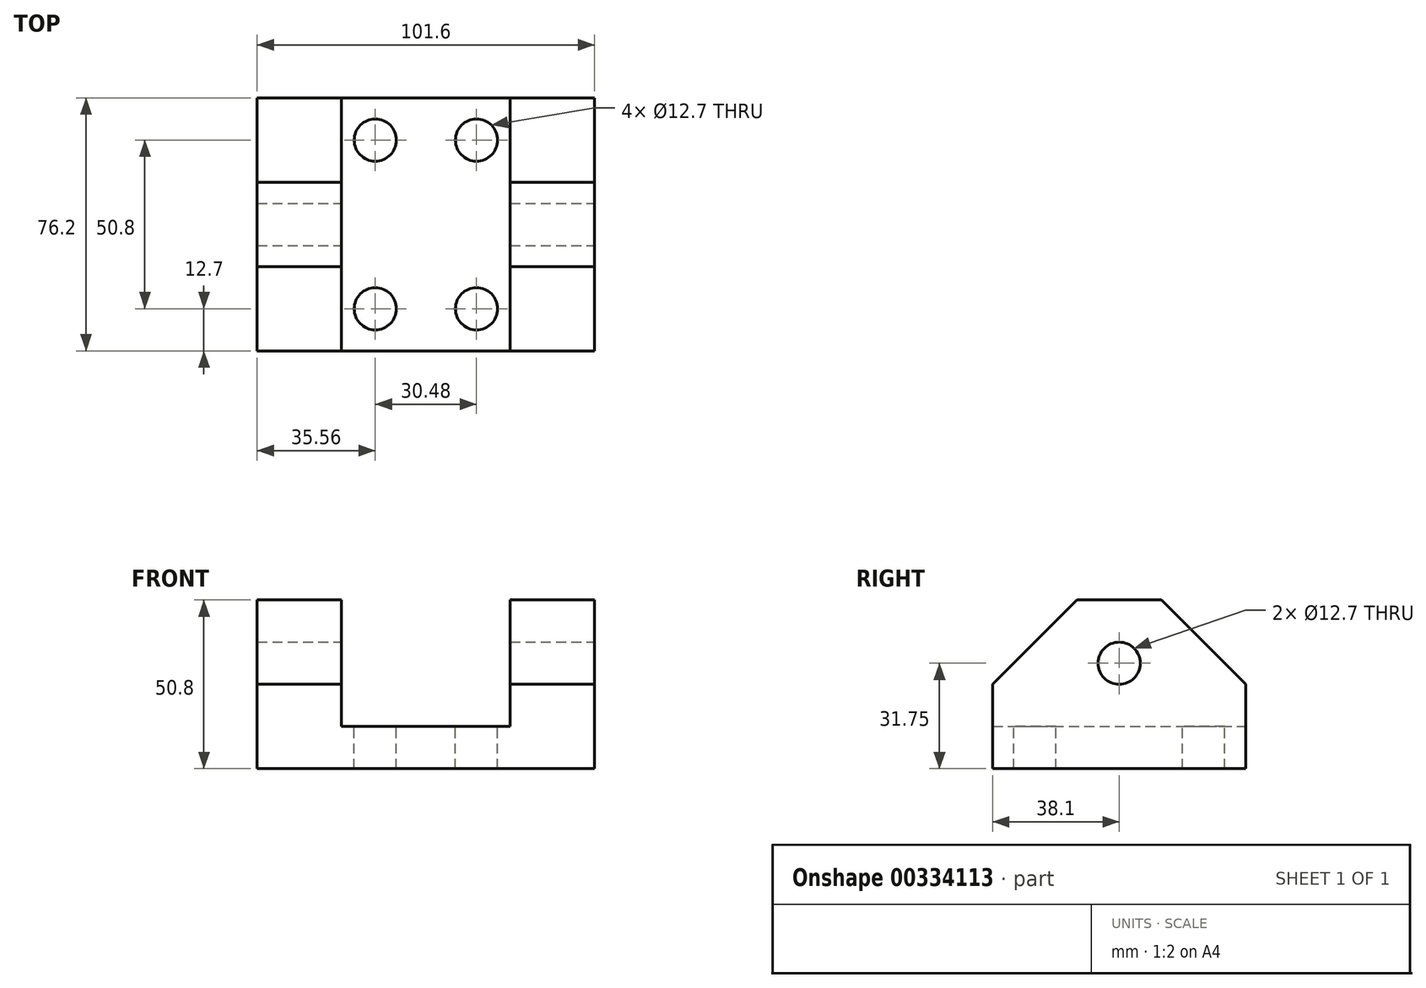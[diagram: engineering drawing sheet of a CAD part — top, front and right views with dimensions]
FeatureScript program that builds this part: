
annotation { "Feature Type Name" : "Feature", "Feature Type Description" : "" }
export const myFeature = defineFeature(function(context is Context, id is Id, definition is map)
    precondition{}
    {
        {
            var Q0;
            Q0=qCreatedBy(makeId("Top.planeOp"),FACE);
            var sketch = newSketch(context, id + "F0", { "sketchPlane" : qUnion([Q0])});
            skLineSegment(sketch, "E0.bottom", {"start": v(-50.8, 38.1) * mm, "end": v(50.8, 38.1) * mm});
            skLineSegment(sketch, "E0.top", {"start": v(-50.8, -38.1) * mm, "end": v(50.8, -38.1) * mm});
            skLineSegment(sketch, "E0.left", {"start": v(-50.8, 38.1) * mm, "end": v(-50.8, -38.1) * mm});
            skLineSegment(sketch, "E0.right", {"start": v(50.8, 38.1) * mm, "end": v(50.8, -38.1) * mm});
            skPoint(sketch, "E0.middle", {"position": v(0, 0) * mm});
            skSolve(sketch);
        }
        {
            var Q0;
            Q0 = qSketchRegion(id + "F0", true);
            extrude(context, id + "F1", {"entities" : qUnion([Q0]), "depth" : 50.8 * mm});
        }
        {
            var Q0;
            Q0=makeQuery(id+"F1.opExtrude","CAP_FACE",FACE,{"disambiguationData":[OSD([sQuery(id+"F0.wireOp",EDGE,"E0.bottom"),sQuery(id+"F0.wireOp",EDGE,"E0.top"),sQuery(id+"F0.wireOp",EDGE,"E0.left"),sQuery(id+"F0.wireOp",EDGE,"E0.right")])],"isStart":false});
            var sketch = newSketch(context, id + "F2", { "sketchPlane" : qUnion([Q0])});
            skLineSegment(sketch, "E1.bottom", {"start": v(-25.4, -38.1) * mm, "end": v(25.4, -38.1) * mm});
            skLineSegment(sketch, "E1.top", {"start": v(-25.4, 38.1) * mm, "end": v(25.4, 38.1) * mm});
            skLineSegment(sketch, "E1.left", {"start": v(-25.4, -38.1) * mm, "end": v(-25.4, 38.1) * mm});
            skLineSegment(sketch, "E1.right", {"start": v(25.4, -38.1) * mm, "end": v(25.4, 38.1) * mm});
            skPoint(sketch, "E1.middle", {"position": v(0, 0) * mm});
            skSolve(sketch);
        }
        {
            var Q0;
            Q0 = qSketchRegion(id + "F2", true);
            extrude(context, id + "F3", {"entities" : qUnion([Q0]), "operationType" : NewBodyOperationType.REMOVE, "oppositeDirection" : true, "depth" : 38.1 * mm});
        }
        {
            var Q0;
            {var subQ0=sQuery(id+"F0.wireOp",EDGE,"E0.left");var subQ1=sQuery(id+"F0.wireOp",EDGE,"E0.top");Q0=makeQuery(id+"F3.boolean.opBoolean","SPLIT",EDGE,{"disambiguationData":[TD([makeQuery(id+"F1.opExtrude","SWEPT_FACE",FACE,{"disambiguationData":[OSD([subQ0])]})])],"derivedFrom":makeQuery(id+"F1.opExtrude","CAP_EDGE",EDGE,{"disambiguationData":[OSD([subQ1])],"isStart":false})});}
            var Q1;
            {var subQ0=sQuery(id+"F0.wireOp",EDGE,"E0.right");var subQ1=sQuery(id+"F0.wireOp",EDGE,"E0.top");Q1=makeQuery(id+"F3.boolean.opBoolean","SPLIT",EDGE,{"disambiguationData":[TD([makeQuery(id+"F1.opExtrude","SWEPT_FACE",FACE,{"disambiguationData":[OSD([subQ0])]})])],"derivedFrom":makeQuery(id+"F1.opExtrude","CAP_EDGE",EDGE,{"disambiguationData":[OSD([subQ1])],"isStart":false})});}
            var Q2;
            {var subQ0=sQuery(id+"F0.wireOp",EDGE,"E0.bottom");var subQ1=sQuery(id+"F0.wireOp",EDGE,"E0.left");Q2=makeQuery(id+"F3.boolean.opBoolean","SPLIT",EDGE,{"disambiguationData":[TD([makeQuery(id+"F1.opExtrude","SWEPT_FACE",FACE,{"disambiguationData":[OSD([subQ1])]})])],"derivedFrom":makeQuery(id+"F1.opExtrude","CAP_EDGE",EDGE,{"disambiguationData":[OSD([subQ0])],"isStart":false})});}
            var Q3;
            {var subQ0=sQuery(id+"F0.wireOp",EDGE,"E0.bottom");var subQ1=sQuery(id+"F0.wireOp",EDGE,"E0.right");Q3=makeQuery(id+"F3.boolean.opBoolean","SPLIT",EDGE,{"disambiguationData":[TD([makeQuery(id+"F1.opExtrude","SWEPT_FACE",FACE,{"disambiguationData":[OSD([subQ1])]})])],"derivedFrom":makeQuery(id+"F1.opExtrude","CAP_EDGE",EDGE,{"disambiguationData":[OSD([subQ0])],"isStart":false})});}
            chamfer(context, id + "F4", {"entities" : qUnion([Q0, Q1, Q2, Q3]), "width" : 25.4 * mm, "tangentPropagation" : true});
        }
        {
            var Q0;
            Q0=makeQuery(id+"F1.opExtrude","SWEPT_FACE",FACE,{"disambiguationData":[OSD([sQuery(id+"F0.wireOp",EDGE,"E0.right")])]});
            var sketch = newSketch(context, id + "F5", { "sketchPlane" : qUnion([Q0])});
            skCircle(sketch, "E2", {"center": v(0, 31.75) * mm, "radius": 6.35 * mm});
            skSolve(sketch);
        }
        {
            var Q0;
            Q0 = qSketchRegion(id + "F5", true);
            extrude(context, id + "F6", {"entities" : qUnion([Q0]), "operationType" : NewBodyOperationType.REMOVE, "endBound" : BoundingType.THROUGH_ALL, "oppositeDirection" : true, "depth" : 25.4 * mm});
        }
        {
            var Q0;
            Q0=makeQuery(id+"F3.boolean.opBoolean","COPY",FACE,{"derivedFrom":makeQuery(id+"F3.opExtrude","CAP_FACE",FACE,{"disambiguationData":[OSD([sQuery(id+"F2.wireOp",EDGE,"E1.bottom"),sQuery(id+"F2.wireOp",EDGE,"E1.top"),sQuery(id+"F2.wireOp",EDGE,"E1.left"),sQuery(id+"F2.wireOp",EDGE,"E1.right")])],"isStart":false})});
            var sketch = newSketch(context, id + "F7", { "sketchPlane" : qUnion([Q0])});
            skCircle(sketch, "E3", {"center": v(-15.24, -25.4) * mm, "radius": 6.35 * mm});
            skCircle(sketch, "E4.0.1.0", {"center": v(-15.24, 25.4) * mm, "radius": 6.35 * mm});
            skCircle(sketch, "E4.1.0.0", {"center": v(15.24, -25.4) * mm, "radius": 6.35 * mm});
            skCircle(sketch, "E4.1.1.0", {"center": v(15.24, 25.4) * mm, "radius": 6.35 * mm});
            skLineSegment(sketch, "E4.direction1", {"start": v(-15.24, -25.4) * mm, "end": v(15.24, -25.4) * mm, "construction": true});
            skLineSegment(sketch, "E4.direction2", {"start": v(-15.24, -25.4) * mm, "end": v(-15.24, 25.4) * mm, "construction": true});
            skSolve(sketch);
        }
        {
            var Q0;
            Q0 = qSketchRegion(id + "F7", true);
            extrude(context, id + "F8", {"entities" : qUnion([Q0]), "operationType" : NewBodyOperationType.REMOVE, "endBound" : BoundingType.UP_TO_NEXT, "oppositeDirection" : true, "depth" : 25.4 * mm});
        }
    });
